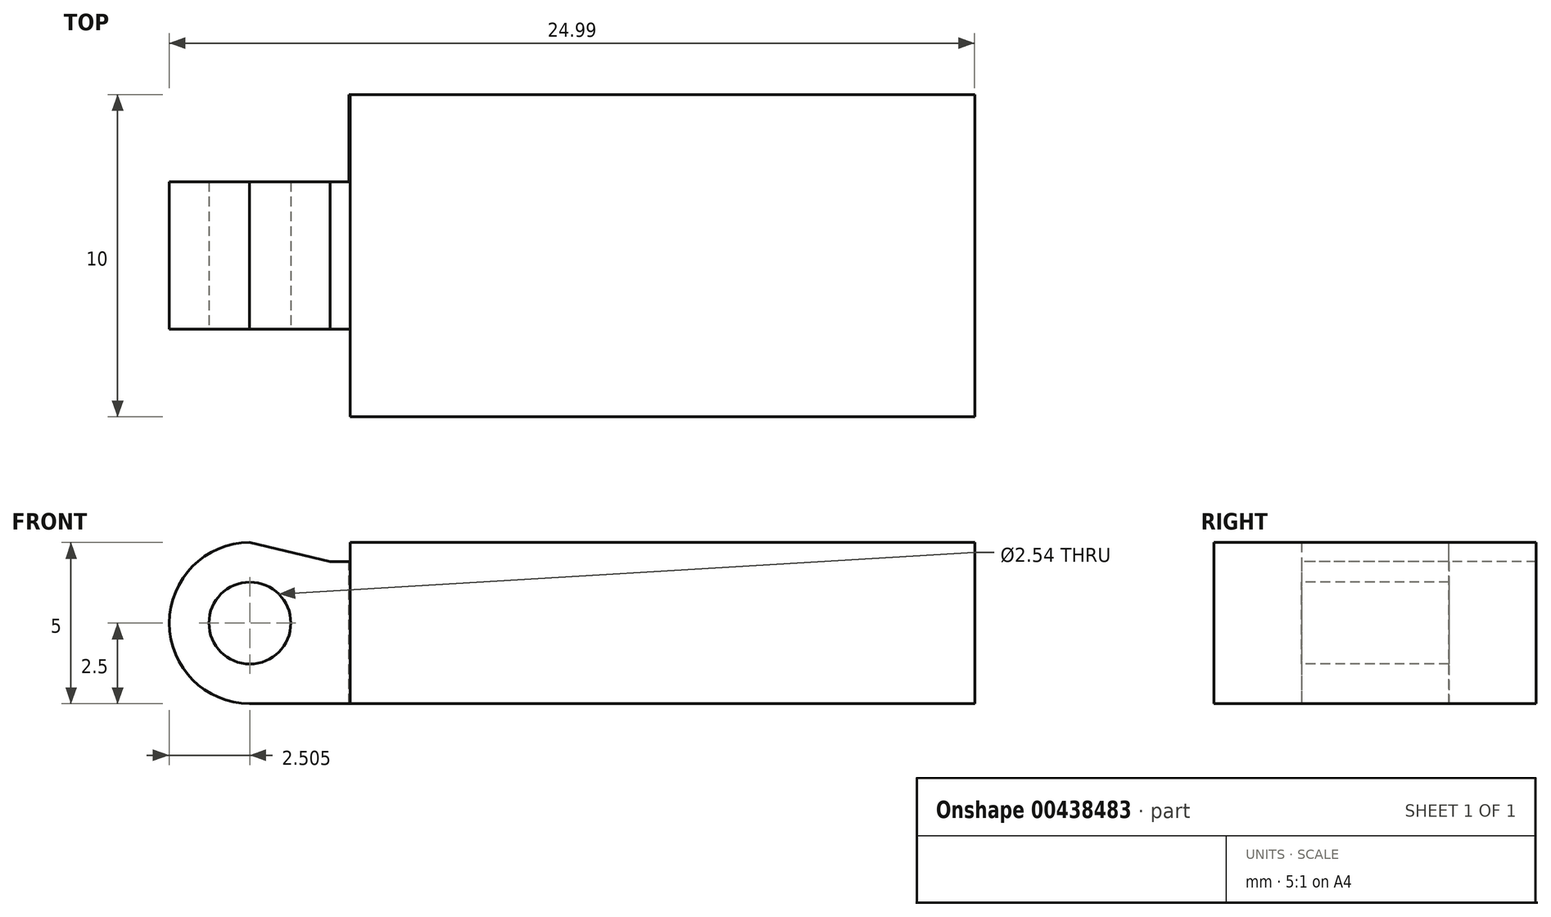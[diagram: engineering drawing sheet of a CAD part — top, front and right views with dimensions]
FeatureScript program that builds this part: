
annotation { "Feature Type Name" : "Feature", "Feature Type Description" : "" }
export const myFeature = defineFeature(function(context is Context, id is Id, definition is map)
    precondition{}
    {
        {
            var Q0;
            Q0=qCreatedBy(makeId("Top.planeOp"),FACE);
            var sketch = newSketch(context, id + "F0", { "sketchPlane" : qUnion([Q0])});
            skLineSegment(sketch, "E0.bottom", {"start": v(-8.96, -1.59) * mm, "end": v(11.04, -1.59) * mm});
            skLineSegment(sketch, "E0.top", {"start": v(-8.96, -11.59) * mm, "end": v(11.04, -11.59) * mm});
            skLineSegment(sketch, "E0.left", {"start": v(-8.96, -1.59) * mm, "end": v(-8.96, -11.59) * mm});
            skLineSegment(sketch, "E0.right", {"start": v(11.04, -1.59) * mm, "end": v(11.04, -11.59) * mm});
            skSolve(sketch);
        }
        {
            var Q0;
            Q0 = qSketchRegion(id + "F0", true);
            extrude(context, id + "F1", {"entities" : qUnion([Q0]), "depth" : 5 * mm});
        }
        {
            var Q0;
            Q0=makeQuery(id+"F1.opExtrude","SWEPT_FACE",FACE,{"disambiguationData":[OSD([sQuery(id+"F0.wireOp",EDGE,"E0.left")])]});
            var sketch = newSketch(context, id + "F2", { "sketchPlane" : qUnion([Q0])});
            skLineSegment(sketch, "E1", {"start": v(6.59, 5) * mm, "end": v(6.59, 0) * mm, "construction": true});
            skLineSegment(sketch, "E2", {"start": v(6.59, 0) * mm, "end": v(4.3, 0) * mm});
            skLineSegment(sketch, "E3", {"start": v(4.3, 0) * mm, "end": v(4.3, 5) * mm});
            skLineSegment(sketch, "E4", {"start": v(4.3, 5) * mm, "end": v(6.59, 5) * mm});
            skLineSegment(sketch, "E5.MirrorCS", {"start": v(8.87, 5) * mm, "end": v(6.59, 5) * mm});
            skLineSegment(sketch, "E6.MirrorCS", {"start": v(8.87, 0) * mm, "end": v(8.87, 5) * mm});
            skLineSegment(sketch, "E7.MirrorCS", {"start": v(6.59, 0) * mm, "end": v(8.87, 0) * mm});
            skSolve(sketch);
        }
        {
            var Q0;
            Q0=makeQuery(id+"F2.imprint","IMPRINT",FACE,{"disambiguationData":[TD([[makeQuery(id+"F2.imprint","IMPRINT",EDGE,{"derivedFrom":sQuery(id+"F2.wireOp",EDGE,"E2")}),1.0]])]});
            extrude(context, id + "F3", {"entities" : qUnion([Q0]), "operationType" : NewBodyOperationType.ADD, "depth" : 5 * mm});
        }
        {
            var Q0;
            Q0=makeQuery(id+"F3.opExtrude","SWEPT_FACE",FACE,{"disambiguationData":[OSD([sQuery(id+"F2.wireOp",EDGE,"E6.MirrorCS")])]});
            var sketch = newSketch(context, id + "F4", { "sketchPlane" : qUnion([Q0])});
            skArc(sketch, "E8", {"start": v(-11.46, 5) * mm, "mid": v(-13.95, 2.5) * mm, "end": v(-11.46, 0) * mm});
            skLineSegment(sketch, "E9", {"start": v(-11.46, 0) * mm, "end": v(-11.64, -0.71) * mm});
            skLineSegment(sketch, "E10", {"start": v(-11.64, -0.71) * mm, "end": v(-15.76, 0.33) * mm});
            skLineSegment(sketch, "E11", {"start": v(-15.76, 0.33) * mm, "end": v(-14.95, 5.58) * mm});
            skLineSegment(sketch, "E12", {"start": v(-14.95, 5.58) * mm, "end": v(-11.46, 5) * mm});
            skCircle(sketch, "E13", {"center": v(-11.45, 2.5) * mm, "radius": 1.27 * mm});
            skSolve(sketch);
        }
        {
            var Q0;
            Q0 = qSketchRegion(id + "F4", true);
            extrude(context, id + "F5", {"entities" : qUnion([Q0]), "operationType" : NewBodyOperationType.REMOVE, "endBound" : BoundingType.THROUGH_ALL, "oppositeDirection" : true, "depth" : 25.4 * mm});
        }
        {
            var Q0;
            Q0=makeQuery(id+"F3.opExtrude","SWEPT_FACE",FACE,{"disambiguationData":[OSD([sQuery(id+"F2.wireOp",EDGE,"E6.MirrorCS")])]});
            var sketch = newSketch(context, id + "F6", { "sketchPlane" : qUnion([Q0])});
            skLineSegment(sketch, "E14", {"start": v(-11.46, 5) * mm, "end": v(-8.96, 4.4) * mm});
            skLineSegment(sketch, "E15", {"start": v(-8.96, 4.4) * mm, "end": v(-8.96, 5) * mm});
            skLineSegment(sketch, "E16", {"start": v(-8.96, 5) * mm, "end": v(-11.46, 5) * mm});
            skSolve(sketch);
        }
        {
            var Q0;
            Q0 = qSketchRegion(id + "F6", true);
            extrude(context, id + "F7", {"entities" : qUnion([Q0]), "operationType" : NewBodyOperationType.REMOVE, "oppositeDirection" : true, "depth" : 25.4 * mm});
        }
        {
            var Q0;
            Q0=makeQuery(id+"F3.opExtrude","SWEPT_FACE",FACE,{"disambiguationData":[OSD([sQuery(id+"F2.wireOp",EDGE,"E6.MirrorCS")])]});
            var sketch = newSketch(context, id + "F8", { "sketchPlane" : qUnion([Q0])});
            skLineSegment(sketch, "E17", {"start": v(-8.96, 4.4) * mm, "end": v(-8.96, 5.17) * mm});
            skLineSegment(sketch, "E18", {"start": v(-8.96, 5.17) * mm, "end": v(-8.34, 5.17) * mm});
            skLineSegment(sketch, "E19", {"start": v(-8.34, 5.17) * mm, "end": v(-8.34, 0) * mm});
            skLineSegment(sketch, "E20", {"start": v(-8.34, 0) * mm, "end": v(-8.96, 0) * mm});
            skLineSegment(sketch, "E21", {"start": v(-8.96, 0) * mm, "end": v(-8.96, 5.17) * mm});
            skSolve(sketch);
        }
        {
            var Q0;
            Q0 = qSketchRegion(id + "F8", true);
            extrude(context, id + "F9", {"entities" : qUnion([Q0]), "operationType" : NewBodyOperationType.REMOVE, "depth" : 25.4 * mm});
        }
        {
            var Q0;
            Q0=makeQuery(id+"F9.boolean.opBoolean","MERGE",FACE,{"derivedFrom":[makeQuery(id+"F3.opExtrude","SWEPT_FACE",FACE,{"disambiguationData":[OSD([sQuery(id+"F2.wireOp",EDGE,"E6.MirrorCS")])]}),makeQuery(id+"F9.opExtrude","CAP_FACE",FACE,{"disambiguationData":[OSD([sQuery(id+"F8.wireOp",EDGE,"E18"),sQuery(id+"F8.wireOp",EDGE,"E19"),sQuery(id+"F8.wireOp",EDGE,"E20"),sQuery(id+"F8.wireOp",EDGE,"E21")])],"isStart":true})]});
            var sketch = newSketch(context, id + "F10", { "sketchPlane" : qUnion([Q0])});
            skLineSegment(sketch, "E22", {"start": v(-8.96, 4.4) * mm, "end": v(-8.34, 4.4) * mm});
            skLineSegment(sketch, "E23", {"start": v(-8.34, 4.4) * mm, "end": v(-8.34, 5) * mm});
            skLineSegment(sketch, "E24", {"start": v(-8.34, 5) * mm, "end": v(-8.96, 5) * mm});
            skLineSegment(sketch, "E25", {"start": v(-8.96, 5) * mm, "end": v(-8.96, 4.4) * mm});
            skSolve(sketch);
        }
        {
            var Q0;
            Q0 = qSketchRegion(id + "F10", true);
            extrude(context, id + "F11", {"entities" : qUnion([Q0]), "operationType" : NewBodyOperationType.REMOVE, "oppositeDirection" : true, "depth" : 25.4 * mm});
        }
        {
            var Q0;
            Q0=makeQuery(id+"F3.opExtrude","SWEPT_FACE",FACE,{"disambiguationData":[OSD([sQuery(id+"F2.wireOp",EDGE,"E3")])]});
            var sketch = newSketch(context, id + "F12", { "sketchPlane" : qUnion([Q0])});
            skLineSegment(sketch, "E26", {"start": v(8.96, 4.4) * mm, "end": v(8.37, 4.4) * mm});
            skLineSegment(sketch, "E27", {"start": v(8.37, 4.4) * mm, "end": v(8.37, -0.13) * mm});
            skLineSegment(sketch, "E28", {"start": v(8.37, -0.13) * mm, "end": v(8.96, -0.13) * mm});
            skLineSegment(sketch, "E29", {"start": v(8.96, -0.13) * mm, "end": v(8.96, 4.4) * mm});
            skSolve(sketch);
        }
        {
            var Q0;
            Q0 = qSketchRegion(id + "F12", true);
            extrude(context, id + "F13", {"entities" : qUnion([Q0]), "operationType" : NewBodyOperationType.REMOVE, "depth" : 25.4 * mm});
        }
    });
